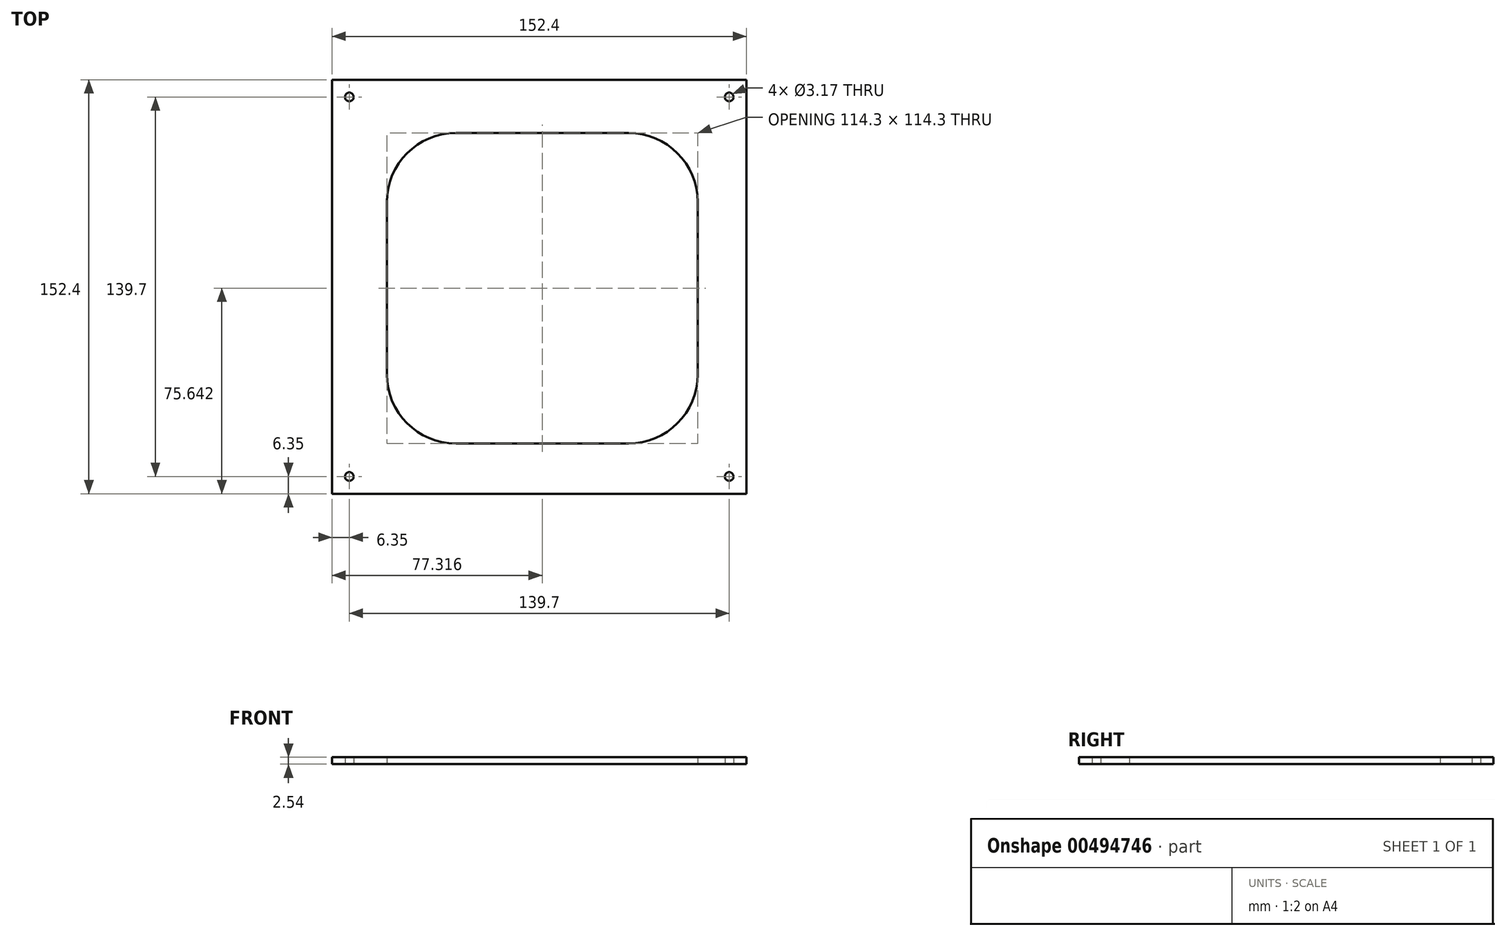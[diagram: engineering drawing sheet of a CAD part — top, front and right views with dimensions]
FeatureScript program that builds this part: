
annotation { "Feature Type Name" : "Feature", "Feature Type Description" : "" }
export const myFeature = defineFeature(function(context is Context, id is Id, definition is map)
    precondition{}
    {
        {
            var Q0;
            Q0=qCreatedBy(makeId("Top.planeOp"),FACE);
            var sketch = newSketch(context, id + "F0", { "sketchPlane" : qUnion([Q0])});
            skLineSegment(sketch, "E0.bottom", {"start": v(76.2, 76.2) * mm, "end": v(-76.2, 76.2) * mm});
            skLineSegment(sketch, "E0.top", {"start": v(76.2, -76.2) * mm, "end": v(-76.2, -76.2) * mm});
            skLineSegment(sketch, "E0.left", {"start": v(76.2, 76.2) * mm, "end": v(76.2, -76.2) * mm});
            skLineSegment(sketch, "E0.right", {"start": v(-76.2, 76.2) * mm, "end": v(-76.2, -76.2) * mm});
            skCircle(sketch, "E1", {"center": v(-69.85, 69.85) * mm, "radius": 1.59 * mm});
            skCircle(sketch, "E2", {"center": v(69.85, 69.85) * mm, "radius": 1.59 * mm});
            skCircle(sketch, "E3", {"center": v(69.85, -69.85) * mm, "radius": 1.59 * mm});
            skCircle(sketch, "E4", {"center": v(-69.85, -69.85) * mm, "radius": 1.59 * mm});
            skLineSegment(sketch, "E5.bottom", {"start": v(-30.63, 56.6) * mm, "end": v(32.87, 56.6) * mm});
            skLineSegment(sketch, "E5.top", {"start": v(-30.63, -57.7) * mm, "end": v(32.87, -57.7) * mm});
            skLineSegment(sketch, "E5.left", {"start": v(-56.03, 31.2) * mm, "end": v(-56.03, -32.3) * mm});
            skLineSegment(sketch, "E5.right", {"start": v(58.27, 31.2) * mm, "end": v(58.27, -32.3) * mm});
            skArc(sketch, "E6.filletArc", {"start": v(-30.63, 56.6) * mm, "mid": v(-48.6, 49.15) * mm, "end": v(-56.03, 31.2) * mm});
            skArc(sketch, "E7.filletArc", {"start": v(58.27, 31.2) * mm, "mid": v(50.83, 49.15) * mm, "end": v(32.87, 56.6) * mm});
            skArc(sketch, "E8.filletArc", {"start": v(32.87, -57.7) * mm, "mid": v(50.83, -50.27) * mm, "end": v(58.27, -32.3) * mm});
            skArc(sketch, "E9.filletArc", {"start": v(-56.03, -32.3) * mm, "mid": v(-48.6, -50.27) * mm, "end": v(-30.63, -57.7) * mm});
            skSolve(sketch);
        }
        {
            var Q0;
            Q0=qSketchRegion(id+"F0",true);
            extrude(context, id + "F1", {"entities" : qUnion([Q0]), "depth" : 2.54 * mm});
        }
    });
